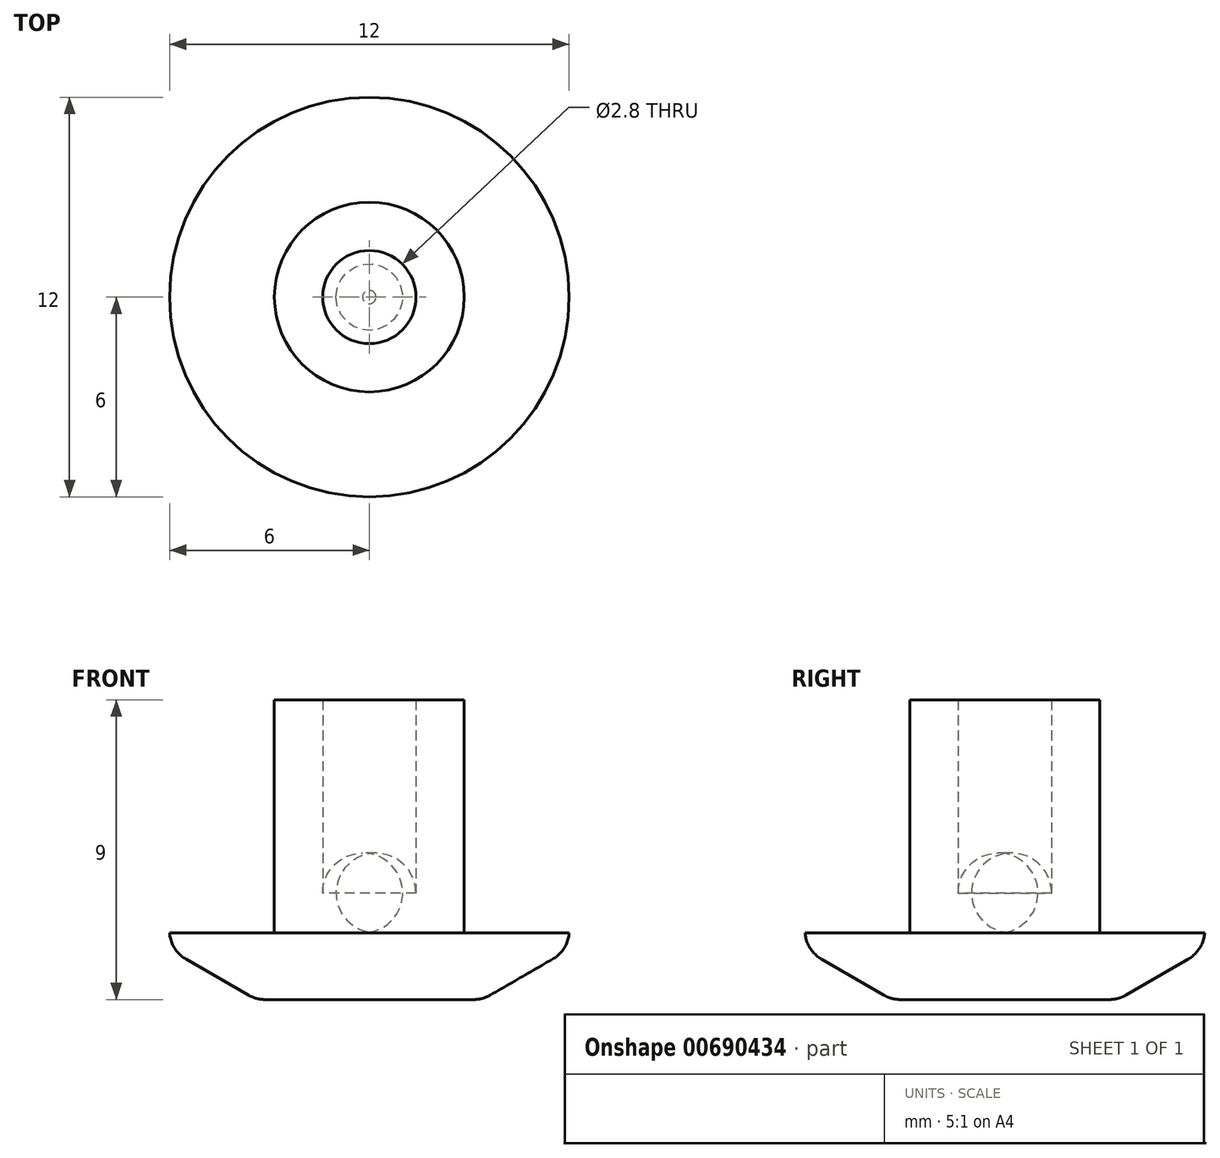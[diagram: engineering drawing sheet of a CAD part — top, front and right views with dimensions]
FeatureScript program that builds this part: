
annotation { "Feature Type Name" : "Feature", "Feature Type Description" : "" }
export const myFeature = defineFeature(function(context is Context, id is Id, definition is map)
    precondition{}
    {
        {
            var Q0;
            Q0=qCreatedBy(makeId("Top.planeOp"),FACE);
            var sketch = newSketch(context, id + "F0", { "sketchPlane" : qUnion([Q0])});
            skCircle(sketch, "E0", {"center": v(0, 0) * mm, "radius": 6 * mm});
            skSolve(sketch);
        }
        {
            var Q0;
            Q0=qSketchRegion(id+"F0",true);
            extrude(context, id + "F1", {"entities" : qUnion([Q0]), "depth" : 2 * mm, "offsetDistance" : 25 * mm});
        }
        {
            var Q0;
            Q0=makeQuery(id+"F1.opExtrude","CAP_EDGE",EDGE,{"disambiguationData":[OSD([sQuery(id+"F0.wireOp",EDGE,"E0")])],"isStart":true});
            chamfer(context, id + "F2", {"entities" : qUnion([Q0]), "chamferType" : ChamferType.OFFSET_ANGLE, "width" : 1.5 * mm, "oppositeDirection" : false, "angle" : 60 * degree, "tangentPropagation" : true});
        }
        {
            var Q0;
            {var subQ0=sQuery(id+"F0.wireOp",EDGE,"E0");Q0=makeQuery(id+"F2.opChamfer","BLEND_EDGE",EDGE,{"blendedFrom":[makeQuery(id+"F1.opExtrude","CAP_EDGE",EDGE,{"disambiguationData":[OSD([subQ0])],"isStart":true}),makeQuery(id+"F1.opExtrude","CAP_FACE",FACE,{"disambiguationData":[OSD([subQ0])],"isStart":true})],"blendedInto":[makeQuery(id+"F1.opExtrude","CAP_FACE",FACE,{"disambiguationData":[OSD([subQ0])],"isStart":true})]});}
            var Q1;
            {var subQ0=sQuery(id+"F0.wireOp",EDGE,"E0");Q1=makeQuery(id+"F2.opChamfer","BLEND_EDGE",EDGE,{"blendedFrom":[makeQuery(id+"F1.opExtrude","CAP_EDGE",EDGE,{"disambiguationData":[OSD([subQ0])],"isStart":true}),makeQuery(id+"F1.opExtrude","SWEPT_FACE",FACE,{"disambiguationData":[OSD([subQ0])]})],"blendedInto":[makeQuery(id+"F1.opExtrude","SWEPT_FACE",FACE,{"disambiguationData":[OSD([subQ0])]})]});}
            fillet(context, id + "F3", {"entities" : qUnion([Q0, Q1]), "radius" : 1 * mm, "tangentPropagation" : true, "allowEdgeOverflow" : false});
        }
        {
            var Q0;
            Q0=makeQuery(id+"F1.opExtrude","CAP_FACE",FACE,{"disambiguationData":[OSD([sQuery(id+"F0.wireOp",EDGE,"E0")])],"isStart":false});
            var sketch = newSketch(context, id + "F4", { "sketchPlane" : qUnion([Q0])});
            skCircle(sketch, "E1", {"center": v(0, 0) * mm, "radius": 2.85 * mm});
            skCircle(sketch, "E2", {"center": v(0, 0) * mm, "radius": 1.4 * mm});
            skSolve(sketch);
        }
        {
            var Q0;
            Q0 = qSketchRegion(id + "F4", true);
            extrude(context, id + "F5", {"entities" : qUnion([Q0]), "operationType" : NewBodyOperationType.ADD, "depth" : 7 * mm, "offsetDistance" : 25 * mm});
        }
        {
            var Q0;
            Q0=makeQuery(id+"F5.opExtrude","CAP_EDGE",EDGE,{"disambiguationData":[OSD([sQuery(id+"F4.wireOp",EDGE,"E2")])],"isStart":true});
            fillet(context, id + "F6", {"entities" : qUnion([Q0]), "radius" : 1.2 * mm, "tangentPropagation" : true, "allowEdgeOverflow" : false});
        }
    });
